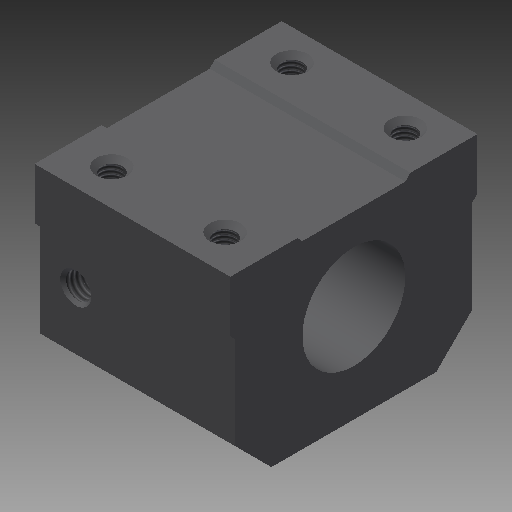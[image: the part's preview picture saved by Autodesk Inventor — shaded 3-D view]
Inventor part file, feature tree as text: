
AUTODESK INVENTOR PART (.ipt)
format: ipt  version: 2018 (Build 220112000, 112)  size: 209,920 bytes
history: native  units: mm
features: sketch x11, other x7, extrude x5, revolve x2, hole x2, pattern_linear x1
ambient origin geometry x8: Origin, YZ Plane, XZ Plane, XY Plane, X Axis, Y Axis, Z Axis, Center Point
bodies: Solid1 (feature_tree)
feature tree (28):
  extrude  "Extrusion1"  Depth=38.0mm TaperAngle=0.0deg
  extrude  "Extrusion2"  TaperAngle=360.0deg  [1 undecoded]
  extrude  "Extrusion3"  Depth=0.8mm TaperAngle=0.0deg
  revolve  "Revolution1"  [1 undecoded]
  revolve  "Revolution2"  [1 undecoded]
  extrude  "Extrusion4"  Depth=24.546069mm
  extrude  "Extrusion5"  Depth=24.546069mm
  hole  "Hole1"  [1 undecoded]
  hole  "Hole2"  [1 undecoded]
  pattern_linear  "Rectangular Pattern1"  Spacing1=1.0mm  [1 undecoded]
  other  "bnt_nut_1_XY"
  other  "bnt_nut_1_YZ"
  other  "bnt_nut_1_ZX"
  other  "bnt_nut_1_X"
  other  "bnt_nut_1_Y"
  other  "bnt_nut_1_Z"
  other  "bnt_nut_1_Center"
  sketch  "Sketch10"  dims[d38=1.15mm d39=20.0mm]
  sketch  "Sketch11"  dims[d41=46.0mm d43=23.0mm d45=1.0mm d46=48.0mm d47=1.0mm d48=36.0mm d49=10.0mm d50=10.0mm d51=20.0mm d52=13.0mm d53=13.0mm d54=32.0mm d55=16.0mm d56=135.0deg d57=18.0mm d58=18.0mm d59=8.0mm d60=6.0mm d61=7.0mm d62=31.0mm]
  sketch  "Sketch_1"  dims[d0=38.0mm d1=0.0mm d2=58.0mm d3=0.0mm]
  sketch  "Sketch_2"  dims[d4=4.6mm d5=0.0mm d6=360.0deg]
  sketch  "Sketch_3"  dims[d7=360.0deg d8=0.8mm d9=0.0mm]
  sketch  "Sketch_4"  dims[d10=0.8mm d11=0.0mm]
  sketch  "Sketch_5"  dims[d12=4.917mm d13=10.5415mm d14=6.0mm d15=2.0mm d16=90.0deg d17=14.140584mm d18=120.0deg]
  sketch  "Sketch_6"  dims[d19=4.134mm d20=10.0mm d21=6.0mm d22=2.0mm d23=90.0deg d24=13.0mm d25=120.0deg d26=20.0mm d28=22.0mm d29=20.0mm d31=35.0mm]
  sketch  "Sketch_7"  dims[d32=0.0mm d33=58.0mm]
  sketch  "Sketch8"  dims[d34=1.15mm d35=24.546069mm]
  sketch  "Sketch9"  dims[d36=4.6mm d37=24.546069mm]
note: 6 required parameter values undecoded (feature->parameter linkage not recoverable at this tier; creation-order binding heuristic only, values carry confidence <= 0.55)